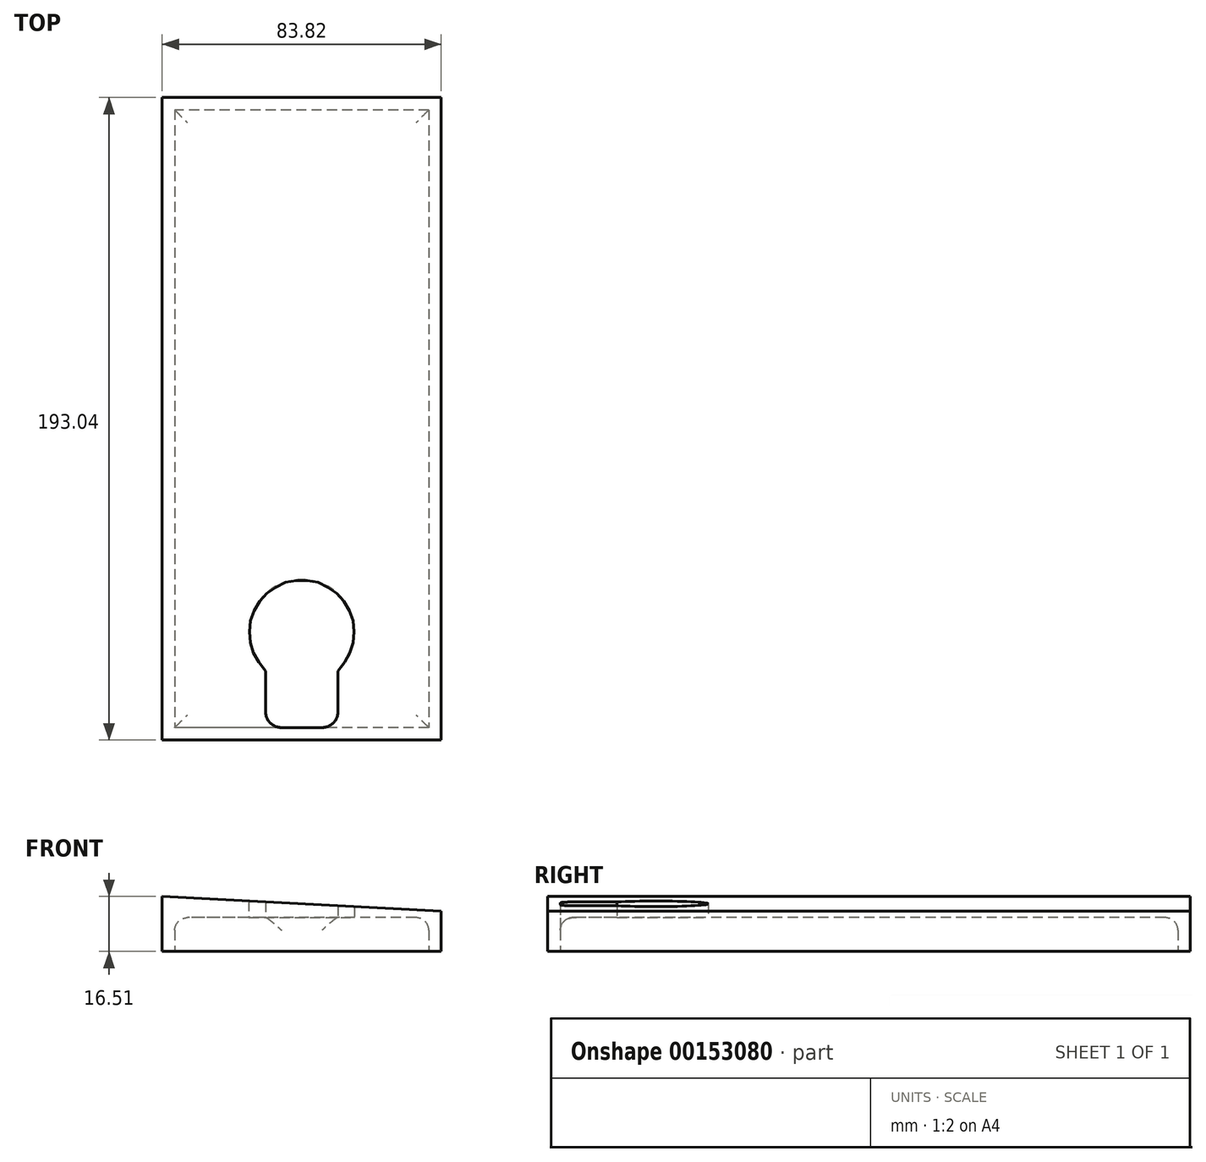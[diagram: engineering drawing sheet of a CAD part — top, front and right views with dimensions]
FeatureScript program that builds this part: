
annotation { "Feature Type Name" : "Feature", "Feature Type Description" : "" }
export const myFeature = defineFeature(function(context is Context, id is Id, definition is map)
    precondition{}
    {
        {
            var Q0;
            Q0=qCreatedBy(makeId("Front.planeOp"),FACE);
            var sketch = newSketch(context, id + "F0", { "sketchPlane" : qUnion([Q0])});
            skLineSegment(sketch, "E0", {"start": v(-7.42, 0) * mm, "end": v(-7.42, 6.35) * mm});
            skLineSegment(sketch, "E1", {"start": v(-7.42, 6.35) * mm, "end": v(76.4, 1.96) * mm});
            skLineSegment(sketch, "E2", {"start": v(76.4, 1.96) * mm, "end": v(76.4, 0) * mm});
            skLineSegment(sketch, "E3", {"start": v(76.4, 0) * mm, "end": v(-7.42, 0) * mm});
            skLineSegment(sketch, "E4", {"start": v(-7.42, 6.35) * mm, "end": v(14, 6.35) * mm, "construction": true});
            skLineSegment(sketch, "E5.bottom", {"start": v(-7.42, 0) * mm, "end": v(76.4, 0) * mm});
            skLineSegment(sketch, "E5.top", {"start": v(-7.42, -10.16) * mm, "end": v(76.4, -10.16) * mm});
            skLineSegment(sketch, "E5.left", {"start": v(-7.42, 0) * mm, "end": v(-7.42, -10.16) * mm});
            skLineSegment(sketch, "E5.right", {"start": v(76.4, 0) * mm, "end": v(76.4, -10.16) * mm});
            skSolve(sketch);
        }
        {
            var Q0;
            Q0 = qSketchRegion(id + "F0", true);
            extrude(context, id + "F1", {"entities" : qUnion([Q0]), "depth" : 193.04 * mm});
        }
        {
            var Q0;
            Q0=makeQuery(id+"F1.opExtrude","SWEPT_FACE",FACE,{"disambiguationData":[OSD([sQuery(id+"F0.wireOp",EDGE,"E5.top")])]});
            var sketch = newSketch(context, id + "F2", { "sketchPlane" : qUnion([Q0])});
            skLineSegment(sketch, "E6.bottom", {"start": v(72.65, 3.75) * mm, "end": v(-3.68, 3.75) * mm});
            skLineSegment(sketch, "E6.top", {"start": v(72.65, 189.3) * mm, "end": v(-3.68, 189.3) * mm});
            skLineSegment(sketch, "E6.left", {"start": v(72.65, 3.75) * mm, "end": v(72.65, 189.3) * mm});
            skLineSegment(sketch, "E6.right", {"start": v(-3.68, 3.75) * mm, "end": v(-3.68, 189.3) * mm});
            skPoint(sketch, "E6.middle", {"position": v(34.49, 96.52) * mm});
            skPoint(sketch, "E6.middle.positionSnap0", {"position": v(34.49, 0) * mm});
            skPoint(sketch, "E6.middle.positionSnap1", {"position": v(-7.42, 96.52) * mm});
            skPoint(sketch, "E6.centerSnap0", {"position": v(34.49, 0) * mm});
            skPoint(sketch, "E6.centerSnap1", {"position": v(-7.42, 96.52) * mm});
            skSolve(sketch);
        }
        {
            var Q0;
            Q0 = qSketchRegion(id + "F2", true);
            extrude(context, id + "F3", {"entities" : qUnion([Q0]), "operationType" : NewBodyOperationType.REMOVE, "oppositeDirection" : true, "depth" : 10.16 * mm});
        }
        {
            var Q0;
            Q0=makeQuery(id+"F3.boolean.opBoolean","COPY",FACE,{"derivedFrom":makeQuery(id+"F3.opExtrude","CAP_FACE",FACE,{"disambiguationData":[OSD([sQuery(id+"F2.wireOp",EDGE,"E6.bottom"),sQuery(id+"F2.wireOp",EDGE,"E6.top"),sQuery(id+"F2.wireOp",EDGE,"E6.left"),sQuery(id+"F2.wireOp",EDGE,"E6.right")])],"isStart":false})});
            var sketch = newSketch(context, id + "F4", { "sketchPlane" : qUnion([Q0])});
            skCircle(sketch, "E7", {"center": v(34.49, 160.72) * mm, "radius": 15.88 * mm});
            skPoint(sketch, "E7.centerSnap0", {"position": v(34.49, 189.3) * mm});
            skLineSegment(sketch, "E8", {"start": v(23.6, 172.28) * mm, "end": v(23.6, 189.3) * mm});
            skLineSegment(sketch, "E9", {"start": v(45.37, 172.28) * mm, "end": v(45.37, 189.3) * mm});
            skLineSegment(sketch, "E10", {"start": v(45.37, 189.3) * mm, "end": v(23.6, 189.3) * mm});
            skSolve(sketch);
        }
        {
            var Q0;
            Q0 = qSketchRegion(id + "F4", true);
            extrude(context, id + "F5", {"entities" : qUnion([Q0]), "operationType" : NewBodyOperationType.REMOVE, "oppositeDirection" : true, "depth" : 25.4 * mm});
        }
        {
            var Q0;
            {var subQ0=sQuery(id+"F2.wireOp",EDGE,"E6.left");var subQ1=sQuery(id+"F2.wireOp",EDGE,"E6.top");Q0=makeQuery(id+"F5.boolean.opBoolean","SPLIT",EDGE,{"disambiguationData":[TD([makeQuery(id+"F3.boolean.opBoolean","COPY",FACE,{"derivedFrom":makeQuery(id+"F3.opExtrude","SWEPT_FACE",FACE,{"disambiguationData":[OSD([subQ0])]})})])],"derivedFrom":makeQuery(id+"F3.boolean.opBoolean","COPY",EDGE,{"derivedFrom":makeQuery(id+"F3.opExtrude","CAP_EDGE",EDGE,{"disambiguationData":[OSD([subQ1])],"isStart":false})})});}
            var Q1;
            {var subQ0=sQuery(id+"F2.wireOp",EDGE,"E6.right");var subQ1=sQuery(id+"F2.wireOp",EDGE,"E6.top");Q1=makeQuery(id+"F5.boolean.opBoolean","SPLIT",EDGE,{"disambiguationData":[TD([makeQuery(id+"F3.boolean.opBoolean","COPY",FACE,{"derivedFrom":makeQuery(id+"F3.opExtrude","SWEPT_FACE",FACE,{"disambiguationData":[OSD([subQ0])]})})])],"derivedFrom":makeQuery(id+"F3.boolean.opBoolean","COPY",EDGE,{"derivedFrom":makeQuery(id+"F3.opExtrude","CAP_EDGE",EDGE,{"disambiguationData":[OSD([subQ1])],"isStart":false})})});}
            var Q2;
            Q2=makeQuery(id+"F3.boolean.opBoolean","COPY",EDGE,{"derivedFrom":makeQuery(id+"F3.opExtrude","CAP_EDGE",EDGE,{"disambiguationData":[OSD([sQuery(id+"F2.wireOp",EDGE,"E6.right")])],"isStart":false})});
            var Q3;
            Q3=makeQuery(id+"F3.boolean.opBoolean","COPY",EDGE,{"derivedFrom":makeQuery(id+"F3.opExtrude","CAP_EDGE",EDGE,{"disambiguationData":[OSD([sQuery(id+"F2.wireOp",EDGE,"E6.left")])],"isStart":false})});
            var Q4;
            Q4=makeQuery(id+"F3.boolean.opBoolean","COPY",EDGE,{"derivedFrom":makeQuery(id+"F3.opExtrude","CAP_EDGE",EDGE,{"disambiguationData":[OSD([sQuery(id+"F2.wireOp",EDGE,"E6.bottom")])],"isStart":false})});
            fillet(context, id + "F6", {"entities" : qUnion([Q0, Q1, Q2, Q3, Q4]), "radius" : 3.8 * mm, "tangentPropagation" : true, "allowEdgeOverflow" : false});
        }
        {
            var Q0;
            Q0=makeQuery(id+"F5.boolean.opBoolean","COPY",EDGE,{"derivedFrom":makeQuery(id+"F5.opExtrude","SWEPT_EDGE",EDGE,{"disambiguationData":[OSD([sQuery(id+"F2.wireOp",EDGE,"E6.top"),sQuery(id+"F4.wireOp",EDGE,"E9"),sQuery(id+"F4.wireOp",EDGE,"E10")])]})});
            var Q1;
            Q1=makeQuery(id+"F5.boolean.opBoolean","COPY",EDGE,{"derivedFrom":makeQuery(id+"F5.opExtrude","SWEPT_EDGE",EDGE,{"disambiguationData":[OSD([sQuery(id+"F2.wireOp",EDGE,"E6.top"),sQuery(id+"F4.wireOp",EDGE,"E8"),sQuery(id+"F4.wireOp",EDGE,"E10")])]})});
            fillet(context, id + "F7", {"entities" : qUnion([Q0, Q1]), "radius" : 4.83 * mm, "tangentPropagation" : true, "allowEdgeOverflow" : false});
        }
    });
